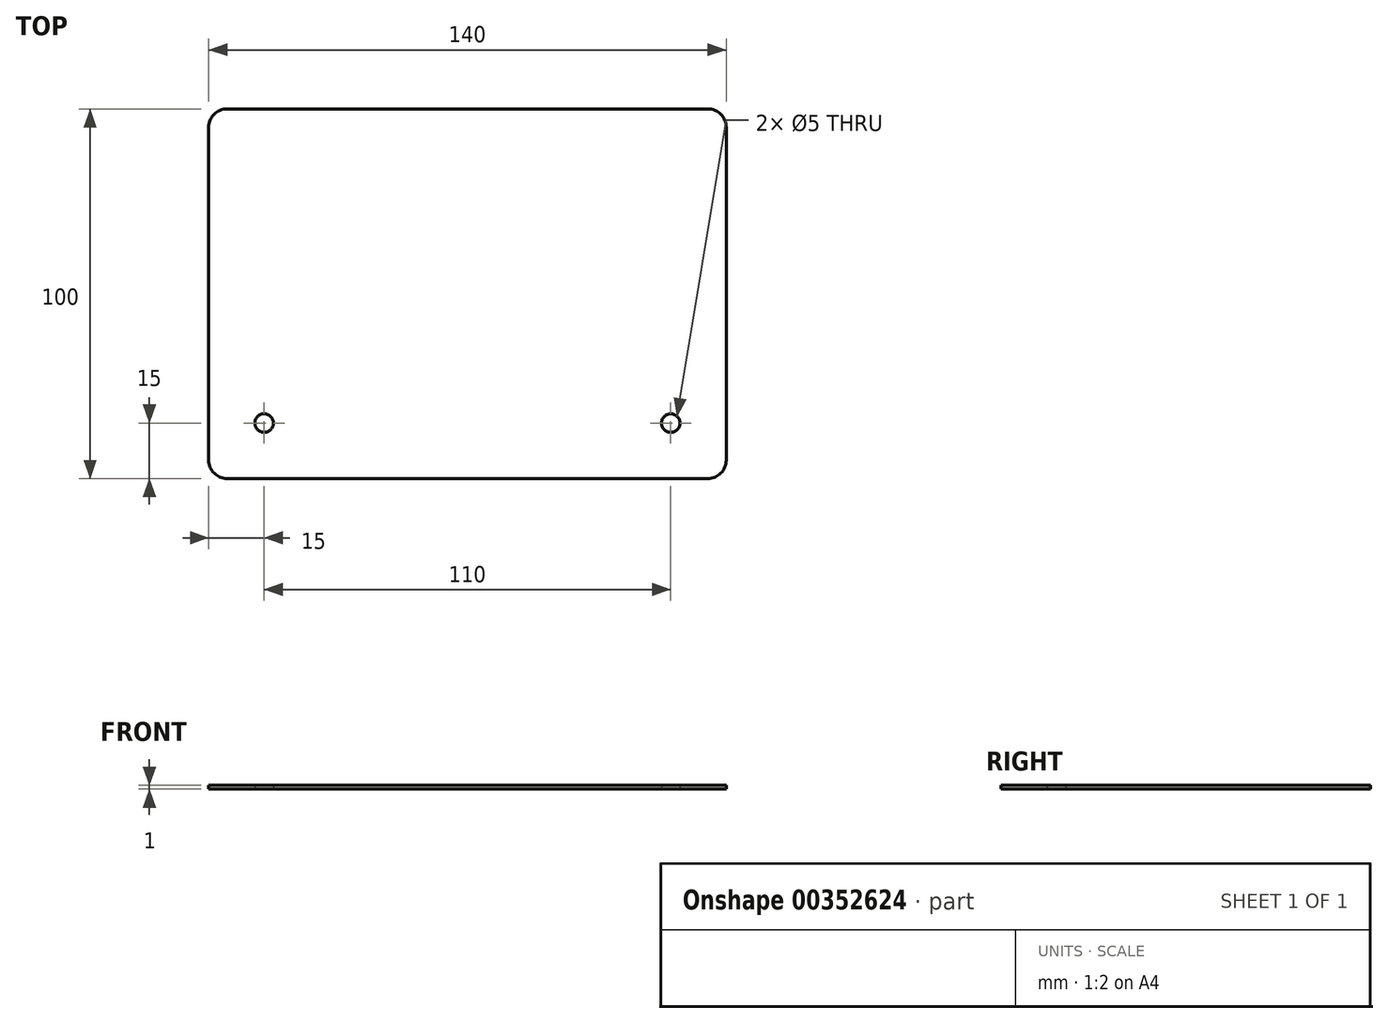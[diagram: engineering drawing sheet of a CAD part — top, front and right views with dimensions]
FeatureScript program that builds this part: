
annotation { "Feature Type Name" : "Feature", "Feature Type Description" : "" }
export const myFeature = defineFeature(function(context is Context, id is Id, definition is map)
    precondition{}
    {
        {
            var Q0;
            Q0=qCreatedBy(makeId("Top.planeOp"),FACE);
            var sketch = newSketch(context, id + "F0", { "sketchPlane" : qUnion([Q0])});
            skLineSegment(sketch, "E0.bottom", {"start": v(65, -50) * mm, "end": v(-65, -50) * mm});
            skLineSegment(sketch, "E0.top", {"start": v(65, 50) * mm, "end": v(-65, 50) * mm});
            skLineSegment(sketch, "E0.left", {"start": v(70, -45) * mm, "end": v(70, 45) * mm});
            skLineSegment(sketch, "E0.right", {"start": v(-70, -45) * mm, "end": v(-70, 45) * mm});
            skPoint(sketch, "E0.middle", {"position": v(0, 0) * mm});
            skPoint(sketch, "E1.visualSharp", {"position": v(-70, 50) * mm});
            skArc(sketch, "E1.filletArc", {"start": v(-65, 50) * mm, "mid": v(-68.54, 48.54) * mm, "end": v(-70, 45) * mm});
            skPoint(sketch, "E2.visualSharp", {"position": v(70, 50) * mm});
            skArc(sketch, "E2.filletArc", {"start": v(70, 45) * mm, "mid": v(68.54, 48.54) * mm, "end": v(65, 50) * mm});
            skPoint(sketch, "E3.visualSharp", {"position": v(70, -50) * mm});
            skArc(sketch, "E3.filletArc", {"start": v(65, -50) * mm, "mid": v(68.54, -48.54) * mm, "end": v(70, -45) * mm});
            skPoint(sketch, "E4.visualSharp", {"position": v(-70, -50) * mm});
            skArc(sketch, "E4.filletArc", {"start": v(-70, -45) * mm, "mid": v(-68.54, -48.54) * mm, "end": v(-65, -50) * mm});
            skCircle(sketch, "E5", {"center": v(-55, -35) * mm, "radius": 2.5 * mm});
            skCircle(sketch, "E6", {"center": v(55, -35) * mm, "radius": 2.5 * mm});
            skSolve(sketch);
        }
        {
            var Q0;
            Q0=qSketchRegion(id+"F0",true);
            extrude(context, id + "F1", {"entities" : qUnion([Q0]), "depth" : 1 * mm});
        }
    });
